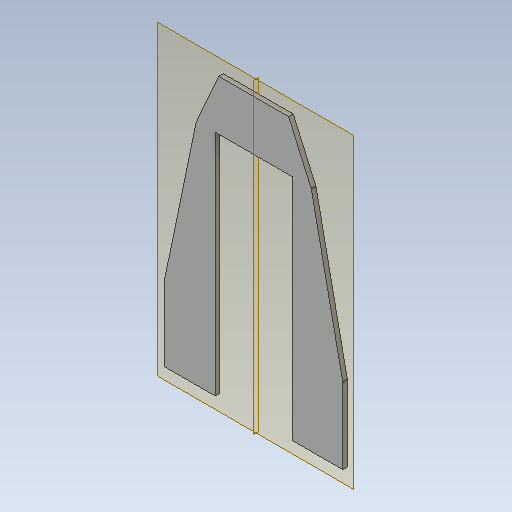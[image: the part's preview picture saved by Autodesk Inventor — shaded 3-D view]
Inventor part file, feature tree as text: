
AUTODESK INVENTOR PART (.ipt)
format: ipt  version: 2020.1 (Build 241239000, 239)  size: 243,200 bytes
history: native  units: mm
features: other x10, sheet_metal_op x3, sketch x3, plane x1, projected_geometry x1
ambient origin geometry x8: Origin, YZ Plane, XZ Plane, XY Plane, X Axis, Y Axis, Z Axis, Center Point
bodies: Solid1 (feature_tree)
feature tree (18):
  plane  "Work Plane1"
  sheet_metal_op  "Face1"
  other  "midtplan"
  other  "modplan parallel med plade"
  sheet_metal_op  "Face2"
  sketch  "Sketch1"  dims[d0=49.0mm]
  other  "Plate1"
  sketch  "Sketch2"  dims[d1=120.0mm]
  projected_geometry  "Projected Loop1"
  sketch  "Sketch4"  dims[d2=35.5mm d3=88.078826mm d4=44.039413mm d5=101.68943mm d6=50.844715mm d7=15.0mm d8=3.0mm d9=2.0mm d10=3.0mm d11=0.0mm d15=1.5mm d16=1.5mm d17=3.0mm d18=3.0mm d19=1.5mm d20=6.0mm d21=3.0mm]
  other  "Plate2"
  sheet_metal_op  "Bend1"
  other  "Cut1"
  other  "Definition1"
  parser-record x1  (decoder bookkeeping rows leaked as tree rows — omitted from the tree; the rows remain in map.json)
  other  "modul.iam"
  other  "stilladssøjle:1"
  other  "rør:1"
note: 1 file-system path scrubbed to <path> (originals preserved in map.json)
